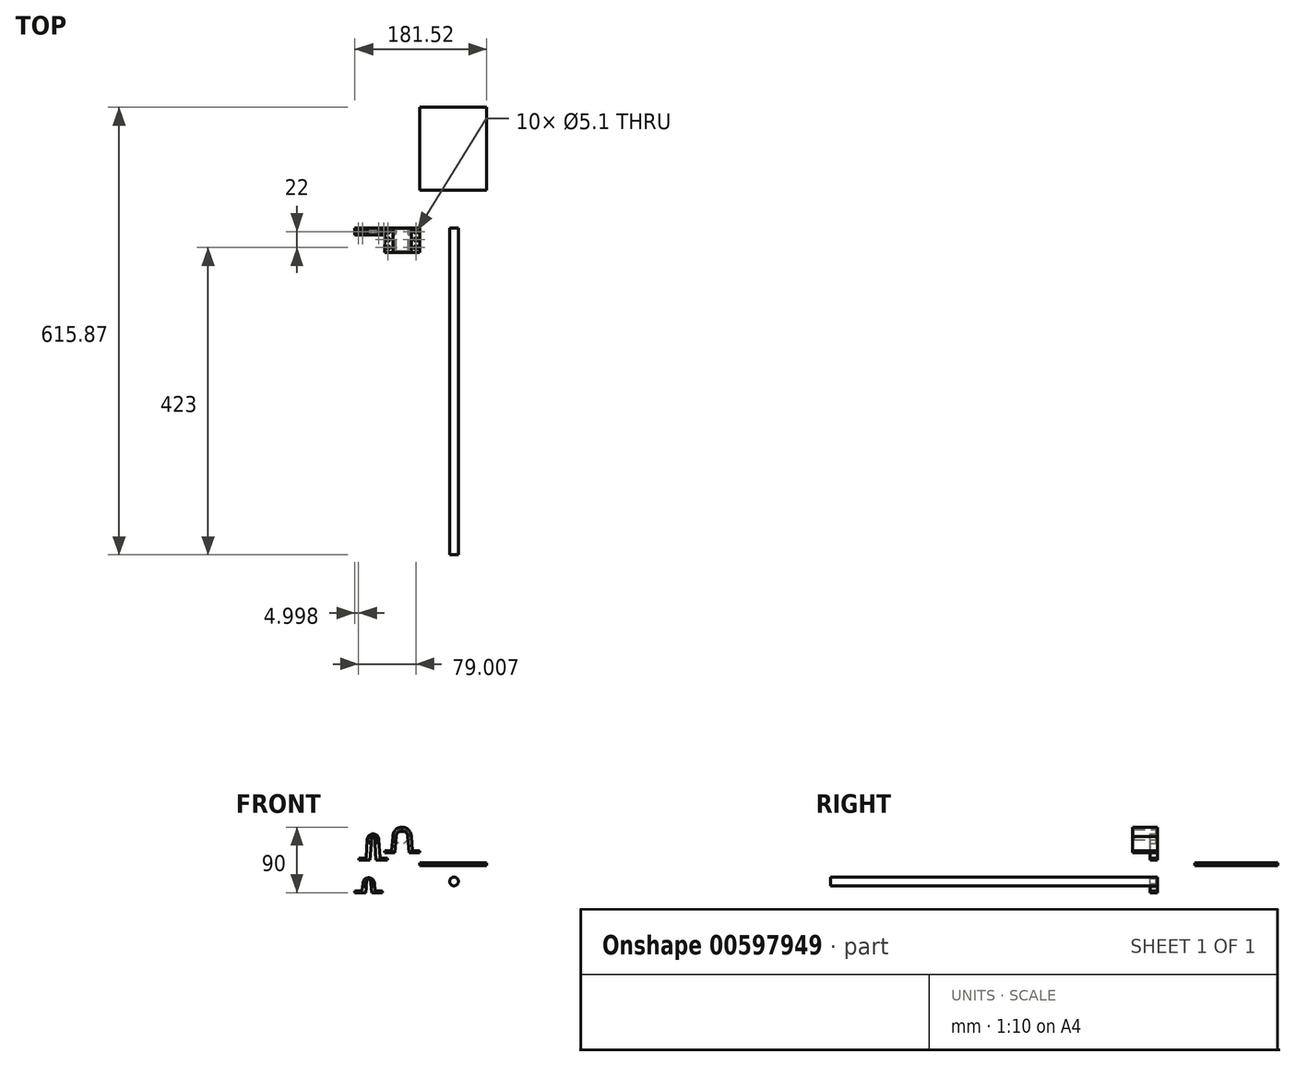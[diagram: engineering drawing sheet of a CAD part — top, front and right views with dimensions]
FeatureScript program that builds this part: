
annotation { "Feature Type Name" : "Feature", "Feature Type Description" : "" }
export const myFeature = defineFeature(function(context is Context, id is Id, definition is map)
    precondition{}
    {
        {
            assignVariable(context, id + "F0", {"name" : "mm", "anyValue" : 10});
        }
        {
            assignVariable(context, id + "F1", {"name" : "minwall", "anyValue" : 2});
        }
        {
            assignVariable(context, id + "F2", {"name" : "bearinglength", "anyValue" : 30});
        }
        {
            var Q0;
            Q0=qCreatedBy(makeId("Front.planeOp"),FACE);
            var sketch = newSketch(context, id + "F3", { "sketchPlane" : qUnion([Q0])});
            skCircle(sketch, "E0", {"center": v(-47.96, 35.54) * mm, "radius": 6 * mm, "construction": true});
            skArc(sketch, "E1", {"start": v(-39.96, 35.54) * mm, "mid": v(-47.96, 43.54) * mm, "end": v(-55.96, 35.54) * mm});
            skLineSegment(sketch, "E2", {"start": v(-53.96, 35.54) * mm, "end": v(-55.96, 35.54) * mm, "construction": true});
            skArc(sketch, "E3", {"start": v(-45.96, 41.2) * mm, "mid": v(-47.96, 41.54) * mm, "end": v(-49.96, 41.2) * mm});
            skPoint(sketch, "E4", {"position": v(-47.96, 41.54) * mm});
            skLineSegment(sketch, "E5", {"start": v(-55.96, 35.54) * mm, "end": v(-57.47, 10.24) * mm});
            skLineSegment(sketch, "E6", {"start": v(-57.47, 10.24) * mm, "end": v(-67.47, 10.24) * mm});
            skLineSegment(sketch, "E7", {"start": v(-67.47, 10.24) * mm, "end": v(-67.47, 7.74) * mm});
            skLineSegment(sketch, "E8", {"start": v(-28.44, 7.74) * mm, "end": v(-28.44, 10.24) * mm});
            skLineSegment(sketch, "E9", {"start": v(-28.44, 10.24) * mm, "end": v(-38.44, 10.24) * mm});
            skLineSegment(sketch, "E10", {"start": v(-38.44, 10.24) * mm, "end": v(-39.96, 35.54) * mm});
            skLineSegment(sketch, "E11", {"start": v(-49.96, 41.2) * mm, "end": v(-51.96, 7.74) * mm});
            skLineSegment(sketch, "E12", {"start": v(-45.96, 41.2) * mm, "end": v(-43.96, 7.74) * mm});
            skLineSegment(sketch, "E13", {"start": v(-67.47, 7.74) * mm, "end": v(-51.96, 7.74) * mm});
            skLineSegment(sketch, "E14", {"start": v(-28.44, 7.74) * mm, "end": v(-43.96, 7.74) * mm});
            skLineSegment(sketch, "E15", {"start": v(-51.96, 7.74) * mm, "end": v(-43.96, 7.74) * mm, "construction": true});
            skPoint(sketch, "E16", {"position": v(-47.96, 7.74) * mm});
            skSolve(sketch);
        }
        {
            var Q0;
            Q0=qCreatedBy(makeId("Front.planeOp"),FACE);
            var sketch = newSketch(context, id + "F4", { "sketchPlane" : qUnion([Q0])});
            skCircle(sketch, "E17", {"center": v(-8.05, 40.1) * mm, "radius": 8 * mm, "construction": true});
            skArc(sketch, "E18", {"start": v(4.63, 40.1) * mm, "mid": v(-8.05, 52.77) * mm, "end": v(-20.72, 40.1) * mm});
            skLineSegment(sketch, "E19", {"start": v(-17.72, 17.6) * mm, "end": v(1.63, 17.6) * mm, "construction": true});
            skPoint(sketch, "E20", {"position": v(-8.05, 17.6) * mm});
            skLineSegment(sketch, "E21", {"start": v(-22.2, 20.1) * mm, "end": v(-20.72, 40.1) * mm});
            skLineSegment(sketch, "E22", {"start": v(4.63, 40.1) * mm, "end": v(6.11, 20.1) * mm});
            skLineSegment(sketch, "E23", {"start": v(-32.2, 17.6) * mm, "end": v(-32.2, 20.1) * mm});
            skLineSegment(sketch, "E24", {"start": v(-32.2, 20.1) * mm, "end": v(-22.2, 20.1) * mm});
            skLineSegment(sketch, "E25", {"start": v(6.11, 20.1) * mm, "end": v(16.11, 20.1) * mm});
            skLineSegment(sketch, "E26", {"start": v(16.11, 20.1) * mm, "end": v(16.11, 17.6) * mm});
            skLineSegment(sketch, "E27", {"start": v(-32.2, 17.6) * mm, "end": v(-17.72, 17.6) * mm});
            skLineSegment(sketch, "E28", {"start": v(1.63, 17.6) * mm, "end": v(16.11, 17.6) * mm});
            skCircle(sketch, "E29", {"center": v(-8.05, 40.1) * mm, "radius": 7 * mm, "construction": true});
            skLineSegment(sketch, "E30", {"start": v(-22.2, 20.1) * mm, "end": v(6.11, 20.1) * mm, "construction": true});
            skPoint(sketch, "E31", {"position": v(-8.05, 20.1) * mm});
            skArc(sketch, "E32", {"start": v(-6.05, 46.8) * mm, "mid": v(-8.05, 47.1) * mm, "end": v(-10.05, 46.8) * mm});
            skCircle(sketch, "E33", {"center": v(-8.05, 40.1) * mm, "radius": 9.5 * mm, "construction": true});
            skLineSegment(sketch, "E34", {"start": v(-10.05, 46.8) * mm, "end": v(-11.67, 47.23) * mm});
            skLineSegment(sketch, "E35", {"start": v(-6.05, 46.8) * mm, "end": v(-4.43, 47.23) * mm});
            skLineSegment(sketch, "E36", {"start": v(-11.67, 47.23) * mm, "end": v(-4.43, 47.23) * mm, "construction": true});
            skPoint(sketch, "E37", {"position": v(-8.05, 47.23) * mm});
            skLineSegment(sketch, "E38", {"start": v(-16.05, 40.1) * mm, "end": v(-17.72, 17.6) * mm});
            skLineSegment(sketch, "E39", {"start": v(1.63, 17.6) * mm, "end": v(-0.05, 40.1) * mm});
            skArc(sketch, "E40", {"start": v(-11.67, 47.23) * mm, "mid": v(-14.72, 44.2) * mm, "end": v(-16.05, 40.1) * mm});
            skArc(sketch, "E41", {"start": v(-0.05, 40.1) * mm, "mid": v(-1.37, 44.2) * mm, "end": v(-4.43, 47.23) * mm});
            skSolve(sketch);
        }
        {
            var Q0;
            Q0=makeQuery(id+"F4.imprint","IMPRINT",FACE,{"disambiguationData":[TD([[makeQuery(id+"F4.imprint","IMPRINT",EDGE,{"derivedFrom":sQuery(id+"F4.wireOp",EDGE,"E18")}),1.0]])]});
            extrude(context, id + "F5", {"entities" : qUnion([Q0]), "depth" : getVariable(context, 'minwall') * mm, "offsetDistance" : 25 * mm});
        }
        {
            var Q0;
            Q0=makeQuery(id+"F5.opExtrude","CAP_FACE",FACE,{"disambiguationData":[OSD([sQuery(id+"F4.wireOp",EDGE,"E18"),sQuery(id+"F4.wireOp",EDGE,"E21"),sQuery(id+"F4.wireOp",EDGE,"E22"),sQuery(id+"F4.wireOp",EDGE,"E23"),sQuery(id+"F4.wireOp",EDGE,"E24"),sQuery(id+"F4.wireOp",EDGE,"E25"),sQuery(id+"F4.wireOp",EDGE,"E26"),sQuery(id+"F4.wireOp",EDGE,"E27"),sQuery(id+"F4.wireOp",EDGE,"E28"),sQuery(id+"F4.wireOp",EDGE,"E32"),sQuery(id+"F4.wireOp",EDGE,"E34"),sQuery(id+"F4.wireOp",EDGE,"E35"),sQuery(id+"F4.wireOp",EDGE,"E38"),sQuery(id+"F4.wireOp",EDGE,"E39"),sQuery(id+"F4.wireOp",EDGE,"E40"),sQuery(id+"F4.wireOp",EDGE,"E41")])],"isStart":false});
            var sketch = newSketch(context, id + "F6", { "sketchPlane" : qUnion([Q0])});
            skPoint(sketch, "E42", {"position": v(-8.05, 40.1) * mm});
            skCircle(sketch, "E43", {"center": v(-8.05, 40.1) * mm, "radius": 6 * mm, "construction": true});
            skArc(sketch, "E44", {"start": v(0.3, 35.54) * mm, "mid": v(-8.05, 49.6) * mm, "end": v(-16.39, 35.54) * mm});
            skLineSegment(sketch, "E45", {"start": v(-16.33, 36.24) * mm, "end": v(-17.72, 17.6) * mm});
            skLineSegment(sketch, "E46", {"start": v(-17.72, 17.6) * mm, "end": v(-32.2, 17.6) * mm});
            skLineSegment(sketch, "E47", {"start": v(-32.2, 17.6) * mm, "end": v(-32.2, 20.1) * mm});
            skLineSegment(sketch, "E48", {"start": v(-32.2, 20.1) * mm, "end": v(-22.2, 20.1) * mm});
            skLineSegment(sketch, "E49", {"start": v(-22.2, 20.1) * mm, "end": v(-20.72, 40.1) * mm});
            skLineSegment(sketch, "E50", {"start": v(0.27, 35.9) * mm, "end": v(1.63, 17.6) * mm});
            skLineSegment(sketch, "E51", {"start": v(1.63, 17.6) * mm, "end": v(16.11, 17.6) * mm});
            skLineSegment(sketch, "E52", {"start": v(16.11, 17.6) * mm, "end": v(16.11, 20.1) * mm});
            skLineSegment(sketch, "E53", {"start": v(16.11, 20.1) * mm, "end": v(6.11, 20.1) * mm});
            skLineSegment(sketch, "E54", {"start": v(6.11, 20.1) * mm, "end": v(4.63, 40.1) * mm});
            skArc(sketch, "E55", {"start": v(4.63, 40.1) * mm, "mid": v(-8.05, 52.77) * mm, "end": v(-20.72, 40.1) * mm});
            skSolve(sketch);
        }
        {
            var Q0;
            Q0=makeQuery(id+"F3.imprint","IMPRINT",FACE,{"disambiguationData":[TD([[makeQuery(id+"F3.imprint","IMPRINT",EDGE,{"derivedFrom":sQuery(id+"F3.wireOp",EDGE,"E1")}),1.0]])]});
            extrude(context, id + "F7", {"entities" : qUnion([Q0]), "depth" : (getVariable(context, 'mm')) * mm, "offsetDistance" : 25 * mm});
        }
        {
            var Q0;
            Q0=makeQuery(id+"F7.opExtrude","CAP_FACE",FACE,{"disambiguationData":[OSD([sQuery(id+"F3.wireOp",EDGE,"E1"),sQuery(id+"F3.wireOp",EDGE,"E3"),sQuery(id+"F3.wireOp",EDGE,"E5"),sQuery(id+"F3.wireOp",EDGE,"E6"),sQuery(id+"F3.wireOp",EDGE,"E7"),sQuery(id+"F3.wireOp",EDGE,"E8"),sQuery(id+"F3.wireOp",EDGE,"E9"),sQuery(id+"F3.wireOp",EDGE,"E10"),sQuery(id+"F3.wireOp",EDGE,"E11"),sQuery(id+"F3.wireOp",EDGE,"E12"),sQuery(id+"F3.wireOp",EDGE,"E13"),sQuery(id+"F3.wireOp",EDGE,"E14")])],"isStart":false});
            var sketch = newSketch(context, id + "F8", { "sketchPlane" : qUnion([Q0])});
            skPoint(sketch, "E56", {"position": v(-47.96, 35.54) * mm});
            skCircle(sketch, "E57", {"center": v(-47.96, 35.54) * mm, "radius": 6.55 * mm});
            skSolve(sketch);
        }
        {
            var Q0;
            {var subQ5=makeQuery(id+"F7.opExtrude","CAP_EDGE",EDGE,{"disambiguationData":[OSD([sQuery(id+"F3.wireOp",EDGE,"E3")])],"isStart":false});Q0=makeQuery(id+"F8.imprint","IMPRINT",FACE,{"disambiguationData":[TD([[makeQuery(id+"F8.imprint","IMPRINT",EDGE,{"derivedFrom":subQ5}),-1.0]])]});}
            extrude(context, id + "F9", {"entities" : qUnion([Q0]), "operationType" : NewBodyOperationType.REMOVE, "oppositeDirection" : true, "depth" : (getVariable(context, 'mm') - getVariable(context, 'minwall')) * mm, "offsetDistance" : 25 * mm});
        }
        {
            var Q0;
            Q0=makeQuery(id+"F6.imprint","IMPRINT",FACE,{"disambiguationData":[TD([[makeQuery(id+"F6.imprint","IMPRINT",EDGE,{"derivedFrom":sQuery(id+"F6.wireOp",EDGE,"E44")}),-1.0]])]});
            extrude(context, id + "F10", {"entities" : qUnion([Q0]), "operationType" : NewBodyOperationType.ADD, "depth" : (getVariable(context, 'bearinglength')) * mm, "offsetDistance" : 25 * mm});
        }
        {
            var Q0;
            Q0=makeQuery(id+"F7.opExtrude","SWEPT_FACE",FACE,{"disambiguationData":[OSD([sQuery(id+"F3.wireOp",EDGE,"E6")])]});
            var sketch = newSketch(context, id + "F11", { "sketchPlane" : qUnion([Q0])});
            skPoint(sketch, "E58", {"position": v(-67.47, -5) * mm});
            skPoint(sketch, "E59", {"position": v(-62.47, -10) * mm});
            skPoint(sketch, "E60", {"position": v(-62.47, -5) * mm});
            skCircle(sketch, "E61", {"center": v(-62.47, -5) * mm, "radius": 2.55 * mm});
            skSolve(sketch);
        }
        {
            var Q0;
            Q0=makeQuery(id+"F7.opExtrude","SWEPT_FACE",FACE,{"disambiguationData":[OSD([sQuery(id+"F3.wireOp",EDGE,"E9")])]});
            var sketch = newSketch(context, id + "F12", { "sketchPlane" : qUnion([Q0])});
            skPoint(sketch, "E62", {"position": v(-38.44, -5) * mm});
            skPoint(sketch, "E63", {"position": v(-33.44, -10) * mm});
            skPoint(sketch, "E64", {"position": v(-33.44, -5) * mm});
            skCircle(sketch, "E65", {"center": v(-33.44, -5) * mm, "radius": 2.55 * mm});
            skSolve(sketch);
        }
        {
            var Q0;
            Q0=makeQuery(id+"F11.imprint","IMPRINT",FACE,{"disambiguationData":[TD([[makeQuery(id+"F11.imprint","IMPRINT",EDGE,{"derivedFrom":sQuery(id+"F11.wireOp",EDGE,"E61")}),1.0]])]});
            extrude(context, id + "F13", {"entities" : qUnion([Q0]), "operationType" : NewBodyOperationType.REMOVE, "endBound" : BoundingType.UP_TO_NEXT, "oppositeDirection" : true, "depth" : 25 * mm, "offsetDistance" : 25 * mm});
        }
        {
            var Q0;
            Q0=makeQuery(id+"F12.imprint","IMPRINT",FACE,{"disambiguationData":[TD([[makeQuery(id+"F12.imprint","IMPRINT",EDGE,{"derivedFrom":sQuery(id+"F12.wireOp",EDGE,"E65")}),1.0]])]});
            extrude(context, id + "F14", {"entities" : qUnion([Q0]), "operationType" : NewBodyOperationType.REMOVE, "endBound" : BoundingType.UP_TO_NEXT, "oppositeDirection" : true, "depth" : 25 * mm, "offsetDistance" : 25 * mm});
        }
        {
            var Q0;
            Q0=makeQuery(id+"FdJSneVe7ETtBZQ_2.boolean.opBoolean","MERGE",FACE,{"derivedFrom":[makeQuery(id+"F10.boolean.opBoolean","MERGE",FACE,{"derivedFrom":[makeQuery(id+"F5.opExtrude","SWEPT_FACE",FACE,{"disambiguationData":[OSD([sQuery(id+"F4.wireOp",EDGE,"E24")])]}),makeQuery(id+"F10.opExtrude","SWEPT_FACE",FACE,{"disambiguationData":[OSD([sQuery(id+"F6.wireOp",EDGE,"E48")])]})]}),makeQuery(id+"FdJSneVe7ETtBZQ_2.opExtrude","SWEPT_FACE",FACE,{"disambiguationData":[OSD([sQuery(id+"FNxvWdAcxwldhFV_2.wireOp",EDGE,"eut7rY8L-FoQD-tY4j-Gk1X-rX6S5ASHvnYD")])]})]});
            var sketch = newSketch(context, id + "F15", { "sketchPlane" : qUnion([Q0])});
            skPoint(sketch, "E66", {"position": v(-27.2, 0) * mm});
            skPoint(sketch, "E67", {"position": v(-27.2, -5) * mm});
            skPoint(sketch, "E68", {"position": v(-27.2, -32) * mm});
            skPoint(sketch, "E69", {"position": v(-27.2, -27) * mm});
            skPoint(sketch, "E70", {"position": v(-32.2, -16) * mm});
            skPoint(sketch, "E71", {"position": v(-27.2, -16) * mm});
            skCircle(sketch, "E72", {"center": v(-27.2, -16) * mm, "radius": 2.55 * mm});
            skCircle(sketch, "E73", {"center": v(-27.2, -5) * mm, "radius": 2.55 * mm});
            skCircle(sketch, "E74", {"center": v(-27.2, -27) * mm, "radius": 2.55 * mm});
            skSolve(sketch);
        }
        {
            var Q0;
            Q0=makeQuery(id+"FdJSneVe7ETtBZQ_2.boolean.opBoolean","MERGE",FACE,{"derivedFrom":[makeQuery(id+"F10.boolean.opBoolean","MERGE",FACE,{"derivedFrom":[makeQuery(id+"F5.opExtrude","SWEPT_FACE",FACE,{"disambiguationData":[OSD([sQuery(id+"F4.wireOp",EDGE,"E25")])]}),makeQuery(id+"F10.opExtrude","SWEPT_FACE",FACE,{"disambiguationData":[OSD([sQuery(id+"F6.wireOp",EDGE,"E53")])]})]}),makeQuery(id+"FdJSneVe7ETtBZQ_2.opExtrude","SWEPT_FACE",FACE,{"disambiguationData":[OSD([sQuery(id+"FNxvWdAcxwldhFV_2.wireOp",EDGE,"8jRSAu6c-GlJO-XiuL-TkVn-E3CeaQiT2mCg")])]})]});
            var sketch = newSketch(context, id + "F16", { "sketchPlane" : qUnion([Q0])});
            skPoint(sketch, "E75", {"position": v(11.11, 0) * mm});
            skPoint(sketch, "E76", {"position": v(11.11, -32) * mm});
            skPoint(sketch, "E77", {"position": v(16.11, -16) * mm});
            skPoint(sketch, "E78", {"position": v(11.11, -16) * mm});
            skPoint(sketch, "E79", {"position": v(11.11, -5) * mm});
            skPoint(sketch, "E80", {"position": v(11.11, -27) * mm});
            skCircle(sketch, "E81", {"center": v(11.11, -16) * mm, "radius": 2.55 * mm});
            skCircle(sketch, "E82", {"center": v(11.11, -5) * mm, "radius": 2.55 * mm});
            skCircle(sketch, "E83", {"center": v(11.11, -27) * mm, "radius": 2.55 * mm});
            skSolve(sketch);
        }
        {
            var Q0;
            Q0=makeQuery(id+"F15.imprint","IMPRINT",FACE,{"disambiguationData":[TD([[makeQuery(id+"F15.imprint","IMPRINT",EDGE,{"derivedFrom":sQuery(id+"F15.wireOp",EDGE,"E73")}),1.0]])]});
            var Q1;
            Q1=makeQuery(id+"F15.imprint","IMPRINT",FACE,{"disambiguationData":[TD([[makeQuery(id+"F15.imprint","IMPRINT",EDGE,{"derivedFrom":sQuery(id+"F15.wireOp",EDGE,"E72")}),1.0]])]});
            var Q2;
            Q2=makeQuery(id+"F15.imprint","IMPRINT",FACE,{"disambiguationData":[TD([[makeQuery(id+"F15.imprint","IMPRINT",EDGE,{"derivedFrom":sQuery(id+"F15.wireOp",EDGE,"E74")}),1.0]])]});
            var Q3;
            Q3=makeQuery(id+"F16.imprint","IMPRINT",FACE,{"disambiguationData":[TD([[makeQuery(id+"F16.imprint","IMPRINT",EDGE,{"derivedFrom":sQuery(id+"F16.wireOp",EDGE,"E83")}),1.0]])]});
            var Q4;
            Q4=makeQuery(id+"F16.imprint","IMPRINT",FACE,{"disambiguationData":[TD([[makeQuery(id+"F16.imprint","IMPRINT",EDGE,{"derivedFrom":sQuery(id+"F16.wireOp",EDGE,"E81")}),1.0]])]});
            var Q5;
            Q5=makeQuery(id+"F16.imprint","IMPRINT",FACE,{"disambiguationData":[TD([[makeQuery(id+"F16.imprint","IMPRINT",EDGE,{"derivedFrom":sQuery(id+"F16.wireOp",EDGE,"E82")}),1.0]])]});
            extrude(context, id + "F17", {"entities" : qUnion([Q0, Q1, Q2, Q3, Q4, Q5]), "operationType" : NewBodyOperationType.REMOVE, "endBound" : BoundingType.UP_TO_NEXT, "oppositeDirection" : true, "depth" : 25 * mm, "offsetDistance" : 25 * mm});
        }
        {
            var Q0;
            Q0=makeQuery(id+"F10.opExtrude","CAP_FACE",FACE,{"disambiguationData":[OSD([sQuery(id+"F4.wireOp",EDGE,"E38"),sQuery(id+"F4.wireOp",EDGE,"E39"),sQuery(id+"F6.wireOp",EDGE,"E44"),sQuery(id+"F6.wireOp",EDGE,"E45"),sQuery(id+"F6.wireOp",EDGE,"E46"),sQuery(id+"F6.wireOp",EDGE,"E47"),sQuery(id+"F6.wireOp",EDGE,"E48"),sQuery(id+"F6.wireOp",EDGE,"E49"),sQuery(id+"F6.wireOp",EDGE,"E50"),sQuery(id+"F6.wireOp",EDGE,"E51"),sQuery(id+"F6.wireOp",EDGE,"E52"),sQuery(id+"F6.wireOp",EDGE,"E53"),sQuery(id+"F6.wireOp",EDGE,"E54"),sQuery(id+"F6.wireOp",EDGE,"E55")])],"isStart":false});
            var sketch = newSketch(context, id + "F18", { "sketchPlane" : qUnion([Q0])});
            skPoint(sketch, "E84", {"position": v(-8.05, 40.1) * mm});
            skPoint(sketch, "E85", {"position": v(-16.05, 40.1) * mm});
            skPoint(sketch, "E86", {"position": v(-0.05, 40.1) * mm});
            skArc(sketch, "E87", {"start": v(-0.05, 40.1) * mm, "mid": v(-8.05, 48.1) * mm, "end": v(-16.05, 40.1) * mm});
            skPoint(sketch, "E88", {"position": v(-20.72, 40.1) * mm});
            skPoint(sketch, "E89", {"position": v(4.63, 40.1) * mm});
            skArc(sketch, "E90", {"start": v(4.63, 40.1) * mm, "mid": v(-8.05, 52.77) * mm, "end": v(-20.72, 40.1) * mm});
            skLineSegment(sketch, "E91", {"start": v(-16.05, 40.1) * mm, "end": v(-17.72, 17.6) * mm});
            skLineSegment(sketch, "E92", {"start": v(-17.72, 17.6) * mm, "end": v(-32.2, 17.6) * mm});
            skLineSegment(sketch, "E93", {"start": v(-32.2, 17.6) * mm, "end": v(-32.2, 20.1) * mm});
            skLineSegment(sketch, "E94", {"start": v(-32.2, 20.1) * mm, "end": v(-22.2, 20.1) * mm});
            skPoint(sketch, "E94.endSnap0", {"position": v(-22.2, 20.1) * mm});
            skLineSegment(sketch, "E95", {"start": v(-22.2, 20.1) * mm, "end": v(-20.72, 40.1) * mm});
            skLineSegment(sketch, "E96", {"start": v(4.63, 40.1) * mm, "end": v(6.11, 20.1) * mm});
            skLineSegment(sketch, "E97", {"start": v(6.11, 20.1) * mm, "end": v(16.11, 20.1) * mm});
            skLineSegment(sketch, "E98", {"start": v(16.11, 20.1) * mm, "end": v(16.11, 17.6) * mm});
            skLineSegment(sketch, "E99", {"start": v(16.11, 17.6) * mm, "end": v(1.63, 17.6) * mm});
            skLineSegment(sketch, "E100", {"start": v(1.63, 17.6) * mm, "end": v(-0.05, 40.1) * mm});
            skPoint(sketch, "E101", {"position": v(6.11, 20.1) * mm});
            skSolve(sketch);
        }
        {
            var Q0;
            {var subQ0=sQuery(id+"F18.wireOp",EDGE,"E87");Q0=makeQuery(id+"F18.imprint","IMPRINT",FACE,{"disambiguationData":[TD([[makeQuery(id+"F18.imprint","IMPRINT",EDGE,{"derivedFrom":subQ0}),-1.0]])]});}
            var Q1;
            Q1=makeQuery(id+"F18.imprint","IMPRINT",FACE,{"disambiguationData":[TD([[makeQuery(id+"F18.imprint","IMPRINT",EDGE,{"derivedFrom":sQuery(id+"F18.wireOp",EDGE,"E90")}),1.0]])]});
            extrude(context, id + "F19", {"entities" : qUnion([Q0, Q1]), "operationType" : NewBodyOperationType.ADD, "depth" : (getVariable(context, 'minwall')) * mm, "offsetDistance" : 25 * mm});
        }
        {
            var Q0;
            Q0=makeQuery(id+"F19.boolean.opBoolean","MERGE",EDGE,{"derivedFrom":[makeQuery(id+"F10.boolean.opBoolean","MERGE",EDGE,{"derivedFrom":[makeQuery(id+"F5.opExtrude","SWEPT_EDGE",EDGE,{"disambiguationData":[OSD([sQuery(id+"F4.wireOp",EDGE,"E22"),sQuery(id+"F4.wireOp",EDGE,"E25")])]}),makeQuery(id+"F10.opExtrude","SWEPT_EDGE",EDGE,{"disambiguationData":[OSD([sQuery(id+"F6.wireOp",EDGE,"E53"),sQuery(id+"F6.wireOp",EDGE,"E54")])]})]}),makeQuery(id+"F19.opExtrude","SWEPT_EDGE",EDGE,{"disambiguationData":[OSD([sQuery(id+"F18.wireOp",EDGE,"E96"),sQuery(id+"F18.wireOp",EDGE,"E97")])]})]});
            var Q1;
            Q1=makeQuery(id+"F7.opExtrude","SWEPT_EDGE",EDGE,{"disambiguationData":[OSD([sQuery(id+"F3.wireOp",EDGE,"E9"),sQuery(id+"F3.wireOp",EDGE,"E10")])]});
            var Q2;
            Q2=makeQuery(id+"F19.boolean.opBoolean","MERGE",EDGE,{"derivedFrom":[makeQuery(id+"F10.boolean.opBoolean","MERGE",EDGE,{"derivedFrom":[makeQuery(id+"F5.opExtrude","SWEPT_EDGE",EDGE,{"disambiguationData":[OSD([sQuery(id+"F4.wireOp",EDGE,"E21"),sQuery(id+"F4.wireOp",EDGE,"E24")])]}),makeQuery(id+"F10.opExtrude","SWEPT_EDGE",EDGE,{"disambiguationData":[OSD([sQuery(id+"F6.wireOp",EDGE,"E48"),sQuery(id+"F6.wireOp",EDGE,"E49")])]})]}),makeQuery(id+"F19.opExtrude","SWEPT_EDGE",EDGE,{"disambiguationData":[OSD([sQuery(id+"F18.wireOp",EDGE,"E94"),sQuery(id+"F18.wireOp",EDGE,"E95")])]})]});
            var Q3;
            Q3=makeQuery(id+"F7.opExtrude","SWEPT_EDGE",EDGE,{"disambiguationData":[OSD([sQuery(id+"F3.wireOp",EDGE,"E5"),sQuery(id+"F3.wireOp",EDGE,"E6")])]});
            fillet(context, id + "F20", {"entities" : qUnion([Q0, Q1, Q2, Q3]), "radius" : 1 * mm, "tangentPropagation" : true, "allowEdgeOverflow" : false});
        }
        {
            var Q0;
            Q0=qCreatedBy(makeId("Front.planeOp"),FACE);
            var sketch = newSketch(context, id + "F21", { "sketchPlane" : qUnion([Q0])});
            skArc(sketch, "E102", {"start": v(-46.06, -24.73) * mm, "mid": v(-54.06, -16.73) * mm, "end": v(-62.06, -24.73) * mm});
            skLineSegment(sketch, "E103", {"start": v(-56.56, -19.27) * mm, "end": v(-58.06, -37.23) * mm});
            skLineSegment(sketch, "E104", {"start": v(-58.06, -37.23) * mm, "end": v(-72.9, -37.23) * mm});
            skLineSegment(sketch, "E105", {"start": v(-72.9, -37.23) * mm, "end": v(-72.9, -34.73) * mm});
            skLineSegment(sketch, "E106", {"start": v(-72.9, -34.73) * mm, "end": v(-62.9, -34.73) * mm});
            skLineSegment(sketch, "E107", {"start": v(-62.9, -34.73) * mm, "end": v(-62.06, -24.73) * mm});
            skLineSegment(sketch, "E108", {"start": v(-51.56, -19.27) * mm, "end": v(-50.06, -37.23) * mm});
            skLineSegment(sketch, "E109", {"start": v(-50.06, -37.23) * mm, "end": v(-35.22, -37.23) * mm});
            skLineSegment(sketch, "E110", {"start": v(-35.22, -37.23) * mm, "end": v(-35.22, -34.73) * mm});
            skLineSegment(sketch, "E111", {"start": v(-45.22, -34.73) * mm, "end": v(-35.22, -34.73) * mm});
            skLineSegment(sketch, "E112", {"start": v(-45.22, -34.73) * mm, "end": v(-46.06, -24.73) * mm});
            skArc(sketch, "E113", {"start": v(-51.56, -19.27) * mm, "mid": v(-54.06, -18.73) * mm, "end": v(-56.56, -19.27) * mm});
            skLineSegment(sketch, "E114", {"start": v(-58.06, -37.23) * mm, "end": v(-50.06, -37.23) * mm, "construction": true});
            skPoint(sketch, "E115", {"position": v(-54.06, -37.23) * mm});
            skPoint(sketch, "E116", {"position": v(-54.06, -18.73) * mm});
            skSolve(sketch);
        }
        {
            var Q0;
            Q0=makeQuery(id+"F21.imprint","IMPRINT",FACE,{"disambiguationData":[TD([[makeQuery(id+"F21.imprint","IMPRINT",EDGE,{"derivedFrom":sQuery(id+"F21.wireOp",EDGE,"E102")}),1.0]])]});
            extrude(context, id + "F22", {"entities" : qUnion([Q0]), "depth" : (getVariable(context, 'mm')) * mm, "offsetDistance" : 25 * mm});
        }
        {
            var Q0;
            Q0=makeQuery(id+"F22.opExtrude","CAP_FACE",FACE,{"disambiguationData":[OSD([sQuery(id+"F21.wireOp",EDGE,"E102"),sQuery(id+"F21.wireOp",EDGE,"E103"),sQuery(id+"F21.wireOp",EDGE,"E104"),sQuery(id+"F21.wireOp",EDGE,"E105"),sQuery(id+"F21.wireOp",EDGE,"E106"),sQuery(id+"F21.wireOp",EDGE,"E107"),sQuery(id+"F21.wireOp",EDGE,"E108"),sQuery(id+"F21.wireOp",EDGE,"E109"),sQuery(id+"F21.wireOp",EDGE,"E110"),sQuery(id+"F21.wireOp",EDGE,"E111"),sQuery(id+"F21.wireOp",EDGE,"E112"),sQuery(id+"F21.wireOp",EDGE,"E113")])],"isStart":false});
            var sketch = newSketch(context, id + "F23", { "sketchPlane" : qUnion([Q0])});
            skPoint(sketch, "E117", {"position": v(-54.06, -24.73) * mm});
            skCircle(sketch, "E118", {"center": v(-54.06, -24.73) * mm, "radius": 6.6 * mm});
            skSolve(sketch);
        }
        {
            var Q0;
            Q0=makeQuery(id+"F22.opExtrude","SWEPT_FACE",FACE,{"disambiguationData":[OSD([sQuery(id+"F21.wireOp",EDGE,"E106")])]});
            var sketch = newSketch(context, id + "F24", { "sketchPlane" : qUnion([Q0])});
            skPoint(sketch, "E119", {"position": v(-72.9, -5) * mm});
            skPoint(sketch, "E120", {"position": v(-67.9, 0) * mm});
            skPoint(sketch, "E121", {"position": v(-67.9, -5) * mm});
            skCircle(sketch, "E122", {"center": v(-67.9, -5) * mm, "radius": 2.55 * mm});
            skSolve(sketch);
        }
        {
            var Q0;
            Q0=makeQuery(id+"F22.opExtrude","SWEPT_FACE",FACE,{"disambiguationData":[OSD([sQuery(id+"F21.wireOp",EDGE,"E111")])]});
            var sketch = newSketch(context, id + "F25", { "sketchPlane" : qUnion([Q0])});
            skPoint(sketch, "E123", {"position": v(-40.22, 0) * mm});
            skPoint(sketch, "E124", {"position": v(-35.22, -5) * mm});
            skPoint(sketch, "E125", {"position": v(-40.22, -5) * mm});
            skCircle(sketch, "E126", {"center": v(-40.22, -5) * mm, "radius": 2.55 * mm});
            skSolve(sketch);
        }
        {
            var Q0;
            Q0=makeQuery(id+"F24.imprint","IMPRINT",FACE,{"disambiguationData":[TD([[makeQuery(id+"F24.imprint","IMPRINT",EDGE,{"derivedFrom":sQuery(id+"F24.wireOp",EDGE,"E122")}),1.0]])]});
            var Q1;
            Q1=makeQuery(id+"F25.imprint","IMPRINT",FACE,{"disambiguationData":[TD([[makeQuery(id+"F25.imprint","IMPRINT",EDGE,{"derivedFrom":sQuery(id+"F25.wireOp",EDGE,"E126")}),1.0]])]});
            extrude(context, id + "F26", {"entities" : qUnion([Q0, Q1]), "operationType" : NewBodyOperationType.REMOVE, "endBound" : BoundingType.UP_TO_NEXT, "oppositeDirection" : true, "depth" : 25 * mm, "offsetDistance" : 25 * mm});
        }
        {
            var Q0;
            Q0=makeQuery(id+"F22.opExtrude","SWEPT_EDGE",EDGE,{"disambiguationData":[OSD([sQuery(id+"F21.wireOp",EDGE,"E106"),sQuery(id+"F21.wireOp",EDGE,"E107")])]});
            var Q1;
            Q1=makeQuery(id+"F22.opExtrude","SWEPT_EDGE",EDGE,{"disambiguationData":[OSD([sQuery(id+"F21.wireOp",EDGE,"E111"),sQuery(id+"F21.wireOp",EDGE,"E112")])]});
            fillet(context, id + "F27", {"entities" : qUnion([Q0, Q1]), "radius" : 1 * mm, "tangentPropagation" : true, "allowEdgeOverflow" : false});
        }
        {
            var Q0;
            {var subQ5=makeQuery(id+"F22.opExtrude","CAP_EDGE",EDGE,{"disambiguationData":[OSD([sQuery(id+"F21.wireOp",EDGE,"E113")])],"isStart":false});Q0=makeQuery(id+"F23.imprint","IMPRINT",FACE,{"disambiguationData":[TD([[makeQuery(id+"F23.imprint","IMPRINT",EDGE,{"derivedFrom":subQ5}),-1.0]])]});}
            extrude(context, id + "F28", {"entities" : qUnion([Q0]), "operationType" : NewBodyOperationType.REMOVE, "oppositeDirection" : true, "depth" : 8 * mm, "offsetDistance" : 25 * mm});
        }
        {
            var Q0;
            Q0=qCreatedBy(makeId("Front.planeOp"),FACE);
            var sketch = newSketch(context, id + "F29", { "sketchPlane" : qUnion([Q0])});
            skCircle(sketch, "E127", {"center": v(63.5, -21.84) * mm, "radius": 6 * mm});
            skSolve(sketch);
        }
        {
            var Q0;
            Q0=makeQuery(id+"F29.imprint","IMPRINT",FACE,{"disambiguationData":[TD([[makeQuery(id+"F29.imprint","IMPRINT",EDGE,{"derivedFrom":sQuery(id+"F29.wireOp",EDGE,"E127")}),1.0]])]});
            extrude(context, id + "F30", {"entities" : qUnion([Q0]), "depth" : 450 * mm, "offsetDistance" : 25 * mm});
        }
        {
            var Q0;
            Q0=qCreatedBy(makeId("Top.planeOp"),FACE);
            var sketch = newSketch(context, id + "F31", { "sketchPlane" : qUnion([Q0])});
            skLineSegment(sketch, "E128.bottom", {"start": v(16.5, 165.87) * mm, "end": v(108.63, 165.87) * mm});
            skLineSegment(sketch, "E128.top", {"start": v(16.5, 51.74) * mm, "end": v(108.63, 51.74) * mm});
            skLineSegment(sketch, "E128.left", {"start": v(16.5, 165.87) * mm, "end": v(16.5, 51.74) * mm});
            skLineSegment(sketch, "E128.right", {"start": v(108.63, 165.87) * mm, "end": v(108.63, 51.74) * mm});
            skSolve(sketch);
        }
        {
            var Q0;
            Q0=makeQuery(id+"F31.imprint","IMPRINT",FACE,{"disambiguationData":[TD([[makeQuery(id+"F31.imprint","IMPRINT",EDGE,{"derivedFrom":sQuery(id+"F31.wireOp",EDGE,"E128.bottom")}),-1.0]])]});
            extrude(context, id + "F32", {"entities" : qUnion([Q0]), "depth" : 4 * mm, "offsetDistance" : 25 * mm});
        }
    });
